# Revit family: Gira_238300
name_source: partatom
category: Elektroinstallationen
revit_build: Autodesk Revit 2017 (Build: 20160225_1515(x64)
units: mm (PartAtom-declared; Revit-internal decimal feet)

## family parameters
Basisbauteil = Fläche
Beim Laden mit Abzugskörper schneiden = Nein
Bemaßung runder Anschluss = Durchmesser verwenden
Beschriftungsausrichtung beibehalten = Nein
Gemeinsam genutzt = Nein
Raumberechnungspunkt = Nein
Teiletyp = Normal

## types (1)
- S3000 Uni-LED-Lstg.zusatz REG Elektronik
    Anzahl der Eingänge = 0
    App-Steuerung über Bluetooth = Nein
    Ausführung der Oberfläche = nicht zutreffend
    BIM = https://media.stage.bim.site X1 REG KNX.rfa
    BIMSITE_PRODUCT_ID = 44f2ea9102cb048f289e55444001b083e8bfdadf
    Beschreibung = System 3000 Universal-LED-Leistungszusatz REG  REG Merkmale:  Schalten und Dimmen von Glühlampen, HV-Halogenlampen, elektronischen Trafos für Halogen-Lampen, induktiven Trafos für Halogen-Lampen, HV-LED- oder Kompaktleuchtstofflampen.  Bedienung erfolgt über vorgeschalteten Dimmer.  Versorgung der angeschlossenen Lasten über gemeinsame Lastleitung.  Elektronischer Übertemperaturschutz.  Hinweise :  Bei höherer Umgebungstemperatur als 45 C ist die angeschlossene Last zu reduzieren.  Die maximale Last und die Anzahl der Leistungszusätze ist abhängig vom Dimmer. Eine Referenzliste finden Sie im Technischen Anhang oder in der Gebrauchsanleitung.
    Breite in Teilungseinheiten = 0
    Bussystem Funkbus = Nein
    Bussystem KNX = Nein
    Bussystem KNX-Funk = Nein
    Bussystem LON = Nein
    Bussystem Powernet = Nein
    Datenblatt = https://media.stage.bim.site
    Datenblatt 1 = https://media.stage.bim.site
    Dimmung Phasenabschnitt = Nein
    Dimmung Phasenanschnitt = Nein
    Funk bidirektional = Nein
    Funktion Schalten = Nein
    GTIN = 4010337031383
    HAN = 238300
    Halogenfrei = Nein
    HeinzeBIM = https://www.heinze.de
    Hersteller = Gira
    Kosten = 0 $
    Lastart = universal und LED Retrofit
    Lichtwertspeicher = Nein
    Max. Anzahl der Jalousieausgänge = 0
    Max. Schaltleistung [Voltampere] = 0
    Mit Beschriftungsfeld = Nein
    Mit Busankopplung = Nein
    Mit LED-Anzeige = Nein
    Montageart = REG
    Nebenstelleneingang = Nein
    Oberfläche Text = sonstige
    Produktseite = https://media.stage.bim.site
    Seriendimmer = Nein
    Transparent = Nein
    Typname = S3000 Uni-LED-Lstg.zusatz REG Elektronik
    URL = https://www.gira.de
    Verwendbar mit Bewegungsmelder = Nein
    Verwendbar mit Funktaste = Nein
    Verwendbar mit IR-Taste = Nein
    Verwendbar mit Präsenzmelder = Nein
    Verwendbar mit Taste = Nein
    Verwendbar mit Zeitschalter/Timer = Nein
    Vor Ort-/Handbedienung = Nein
    Vorgabe-Ansicht = 1219 mm
    Werkstoff Text = sonstige
    Werkstoffgüte = sonstige

## geometry (parser evidence)
native form markers: Sweep x2
no freeform markers — native parametric forms only
